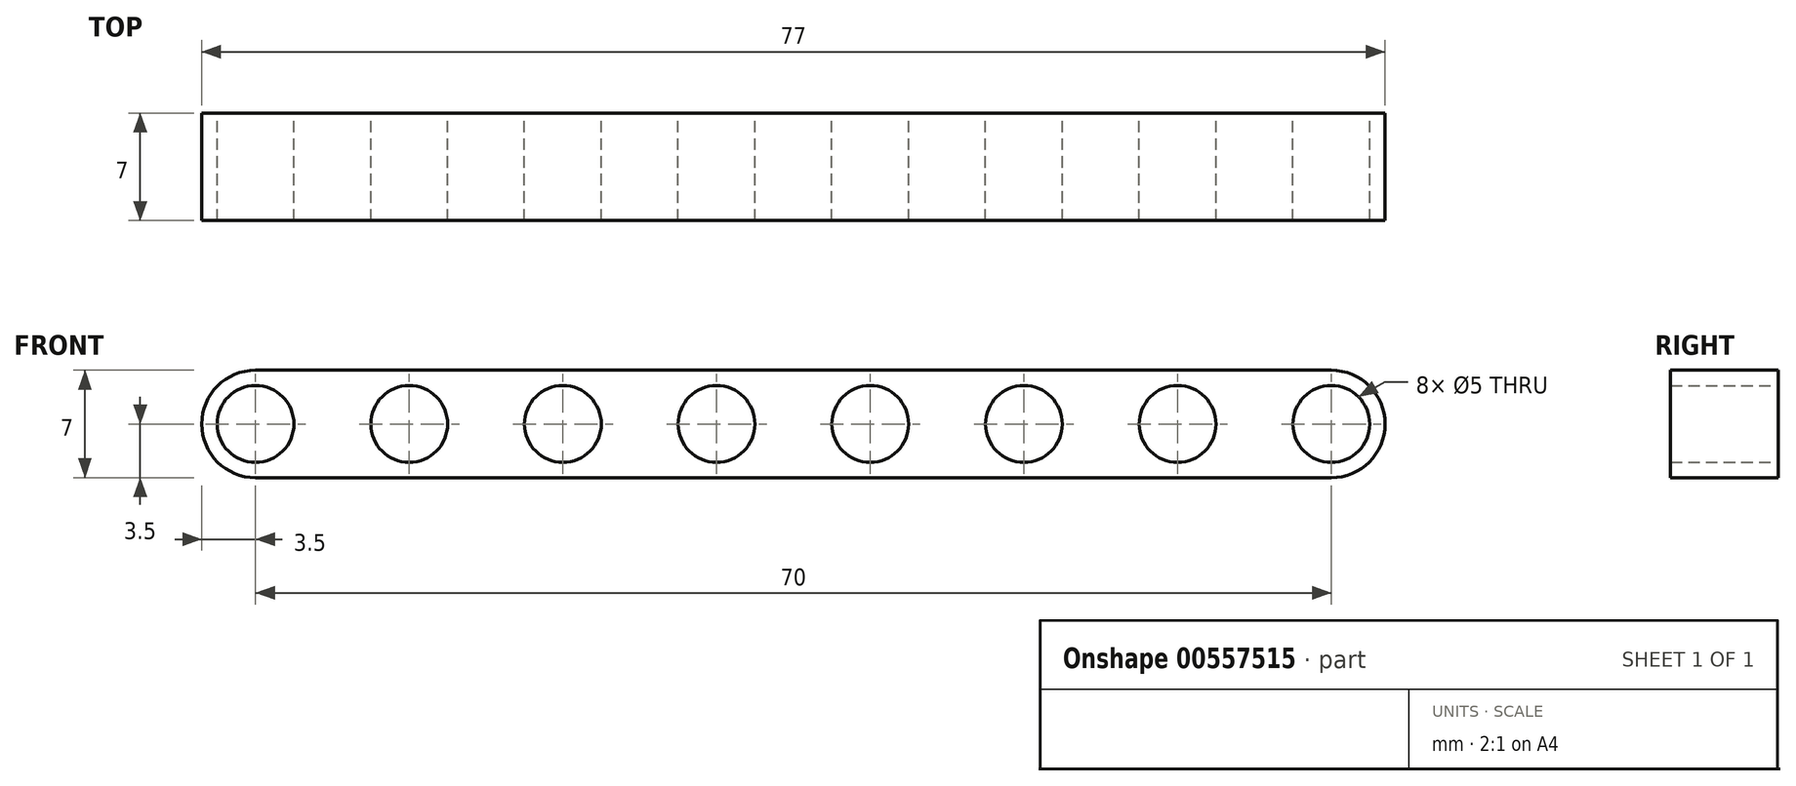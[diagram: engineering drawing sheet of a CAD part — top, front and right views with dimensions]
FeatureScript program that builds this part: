
annotation { "Feature Type Name" : "Feature", "Feature Type Description" : "" }
export const myFeature = defineFeature(function(context is Context, id is Id, definition is map)
    precondition{}
    {
        {
            var Q0;
            Q0=qCreatedBy(makeId("Front.planeOp"),FACE);
            var sketch = newSketch(context, id + "F0", { "sketchPlane" : qUnion([Q0])});
            skLineSegment(sketch, "E0.bottom", {"start": v(-35, 3.5) * mm, "end": v(35, 3.5) * mm});
            skLineSegment(sketch, "E0.top", {"start": v(-35, -3.5) * mm, "end": v(35, -3.5) * mm});
            skPoint(sketch, "E0.middle", {"position": v(0, 0) * mm});
            skArc(sketch, "E1", {"start": v(-35, 3.5) * mm, "mid": v(-38.5, 0) * mm, "end": v(-35, -3.5) * mm});
            skArc(sketch, "E2", {"start": v(35, -3.5) * mm, "mid": v(38.5, 0) * mm, "end": v(35, 3.5) * mm});
            skCircle(sketch, "E3", {"center": v(-35, 0) * mm, "radius": 2.5 * mm});
            skCircle(sketch, "E4.1.0.0", {"center": v(-25, 0) * mm, "radius": 2.5 * mm});
            skCircle(sketch, "E4.2.0.0", {"center": v(-15, 0) * mm, "radius": 2.5 * mm});
            skCircle(sketch, "E4.3.0.0", {"center": v(-5, 0) * mm, "radius": 2.5 * mm});
            skCircle(sketch, "E4.4.0.0", {"center": v(5, 0) * mm, "radius": 2.5 * mm});
            skCircle(sketch, "E4.5.0.0", {"center": v(15, 0) * mm, "radius": 2.5 * mm});
            skCircle(sketch, "E4.6.0.0", {"center": v(25, 0) * mm, "radius": 2.5 * mm});
            skCircle(sketch, "E4.7.0.0", {"center": v(35, 0) * mm, "radius": 2.5 * mm});
            skLineSegment(sketch, "E4.direction1", {"start": v(-35, 0) * mm, "end": v(-25, 0) * mm, "construction": true});
            skSolve(sketch);
        }
        {
            var Q0;
            Q0=makeQuery(id+"F0.imprint","IMPRINT",FACE,{"disambiguationData":[TD([[makeQuery(id+"F0.imprint","IMPRINT",EDGE,{"derivedFrom":sQuery(id+"F0.wireOp",EDGE,"E0.bottom")}),-1.0]])]});
            extrude(context, id + "F1", {"entities" : qUnion([Q0]), "depth" : 7 * mm, "offsetDistance" : 25 * mm});
        }
    });
